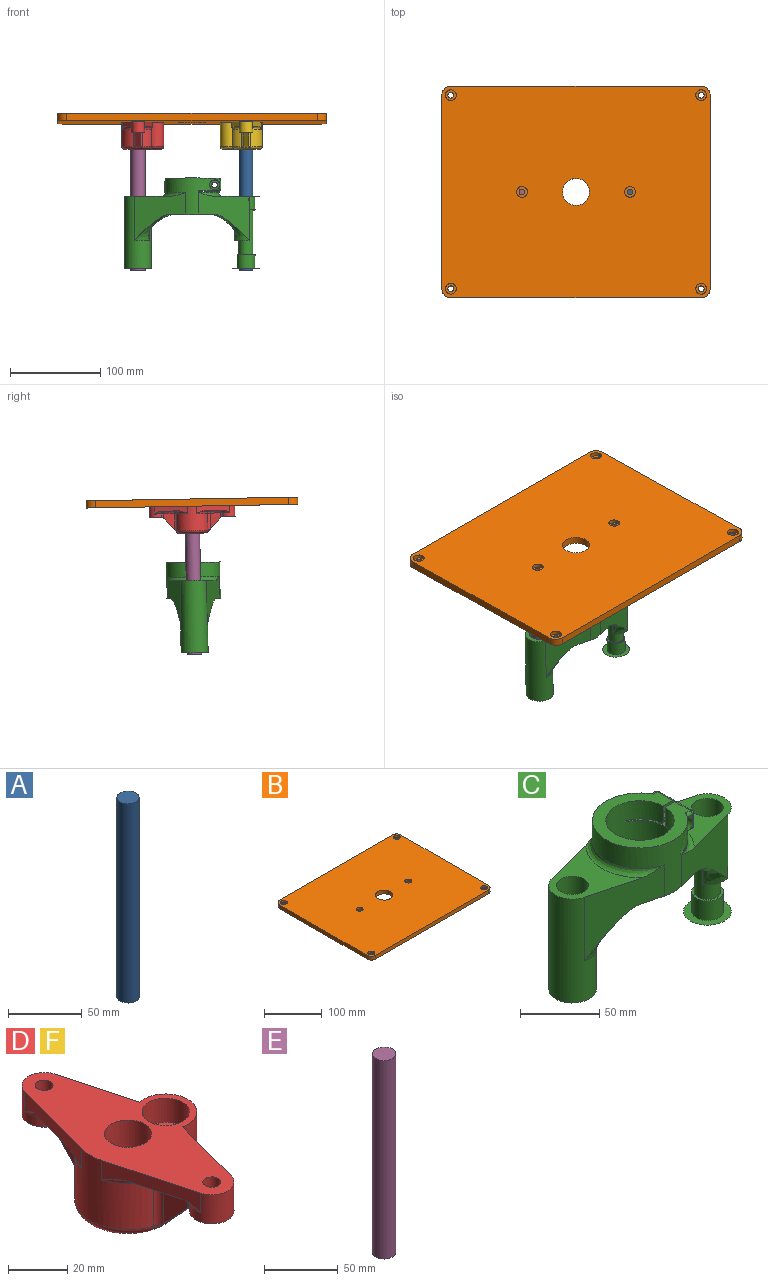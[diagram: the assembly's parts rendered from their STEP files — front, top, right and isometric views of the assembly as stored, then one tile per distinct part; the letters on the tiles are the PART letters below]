
ASSEMBLY  parts=6 mates=6
PART A: 3 faces, bbox 15x15x165 mm
  f0: cylinder r=7.5mm len=165mm, axis (0,0,1), area 7775.4mm2, adj f1,f2
  f1: plane 15x15mm, normal (0,0,1), area 176.7mm2, adj f0
  f2: plane 15x15mm, normal (0,0,-1), area 176.7mm2, adj f0
PART B: 29 faces, bbox 298x235x8 mm
  f0: plane 278x8mm, normal (0,1,0), area 2224mm2, adj f1,f12,f15,f16
  f1: cylinder r=10mm len=10mm, axis (0,0,1), area 125.7mm2, adj f0,f2,f15,f16
  f2: plane 215x8mm, normal (-1,0,0), area 1720mm2, adj f1,f3,f15,f16
  f3: cylinder r=10mm len=10mm, axis (0,0,1), area 125.7mm2, adj f2,f4,f15,f16
  f4: plane 278x8mm, normal (0,-1,0), area 2224mm2, adj f3,f5,f15,f16
  f5: cylinder r=10mm len=10mm, axis (0,0,1), area 125.7mm2, adj f4,f6,f15,f16
  f6: plane 215x8mm, normal (1,0,0), area 1720mm2, adj f5,f12,f15,f16
  f7: cylinder r=6mm len=12mm, axis (0,0,1), area 150.8mm2, adj f15,f20
  f8: cylinder r=6mm len=12mm, axis (0,0,1), area 150.8mm2, adj f15,f24
  f9: cylinder r=6mm len=12mm, axis (0,0,1), area 150.8mm2, adj f15,f22
  f10: cylinder r=6mm len=12mm, axis (0,0,1), area 150.8mm2, adj f15,f18
  f11: cylinder r=15mm len=30mm, axis (0,0,1), area 754mm2, adj f15,f16
  f12: cylinder r=10mm len=10mm, axis (0,0,1), area 125.7mm2, adj f0,f6,f15,f16
  f13: cylinder r=6mm len=12mm, axis (0,0,1), area 150.8mm2, adj f15,f26
  f14: cylinder r=6mm len=12mm, axis (0,0,1), area 150.8mm2, adj f15,f28
  f15: plane 298x235mm, normal (0,0,1), area 68558.7mm2, adj f0,f1,f2,f3,f4,f5,f6,f7
  f16: plane 298x235mm, normal (0,0,-1), area 69038.2mm2, adj f0,f1,f2,f3,f4,f5,f6,f11
  f17: cylinder r=3.25mm len=6.5mm, axis (0,0,1), area 81.7mm2, adj f16,f18
  f18: plane 12x12mm, normal (0,0,1), area 79.9mm2, adj f10,f17
  f19: cylinder r=3.25mm len=6.5mm, axis (0,0,1), area 81.7mm2, adj f16,f20
  f20: plane 12x12mm, normal (0,0,1), area 79.9mm2, adj f7,f19
  f21: cylinder r=3.25mm len=6.5mm, axis (0,0,1), area 81.7mm2, adj f16,f22
  f22: plane 12x12mm, normal (0,0,1), area 79.9mm2, adj f9,f21
  f23: cylinder r=3.25mm len=6.5mm, axis (0,0,1), area 81.7mm2, adj f16,f24
  f24: plane 12x12mm, normal (0,0,1), area 79.9mm2, adj f8,f23
  f25: cylinder r=3.25mm len=6.5mm, axis (0,0,1), area 81.7mm2, adj f16,f26
  f26: plane 12x12mm, normal (0,0,1), area 79.9mm2, adj f13,f25
  f27: cylinder r=3.25mm len=6.5mm, axis (0,0,1), area 81.7mm2, adj f16,f28
  f28: plane 12x12mm, normal (0,0,1), area 79.9mm2, adj f14,f27
PART C: 91 faces, bbox 210x148.6x160 mm
  f0: plane 4.53x2.61mm, normal (0,1,0), area 5.9mm2, adj f1,f89,f90
  f1: cylinder r=2mm len=10mm, axis (0,0,1), area 31.4mm2, adj f0,f2,f85,f86,f87,f88
  f2: plane 5.77x5mm, normal (-1,0,0), area 28.9mm2, adj f1,f3,f84,f90
  f3: plane 11.55x10mm, normal (0,1,0), area 55.4mm2, adj f2,f4,f81,f82,f83,f84,f90
  f4: cylinder r=3.15mm len=10.58mm, axis (0,-1,0), area 209.5mm2, adj f3,f5
  f5: plane 12x10.52mm, normal (0,-1,0), area 94.2mm2, adj f4,f6,f78,f79,f80,f87
  f6: plane 60x60mm, normal (0,0,1), area 1394mm2, adj f5,f7,f26,f27,f28,f78,f80,f89
  f7: plane 14x10.52mm, normal (0,1,0), area 114.4mm2, adj f6,f8,f23,f24,f25,f26,f80
  f8: plane 28.17x23mm, normal (0,0,-1), area 292.9mm2, adj f7,f9,f15,f23,f28,f80
  f9: plane 8.84x1mm, normal (1,0,0), area 8.8mm2, adj f8,f10,f28,f80
  f10: plane 58.34x23mm, normal (0,0,1), area 567.1mm2, adj f9,f11,f28,f80
  f11: plane 8.84x1mm, normal (1,0,0), area 8.8mm2, adj f10,f12,f28,f80
  f12: plane 26.17x23mm, normal (0,0,-1), area 275.7mm2, adj f11,f13,f14,f28,f79,f80
  f13: cylinder r=2mm len=13.58mm, axis (0,-1,0), area 39.5mm2, adj f12,f79,f86,f87
  f14: cylinder r=2mm len=4.77mm, axis (1,0,0), area 12.8mm2, adj f12,f28,f84,f85,f86
  f15: cylinder r=2mm len=4.83mm, axis (1,0,0), area 12.5mm2, adj f8,f16,f21,f22,f28
  f16: cylinder r=5.5mm len=11.22mm, axis (0,-1,0), area 244.7mm2, adj f15,f17,f18,f20,f21,f28
  f17: plane 11x11mm, normal (0,-1,0), area 63.9mm2, adj f16,f25
  f18: cylinder r=2mm len=10mm, axis (0,0,-1), area 29.9mm2, adj f16,f19,f20,f21,f22,f24
  f19: sphere r=2mm, area 6.3mm2, adj f18,f26,f27
  f20: plane 5x3.21mm, normal (0,-1,0), area 4.5mm2, adj f16,f18,f27
  f21: plane 2.21x1.84mm, normal (0,-1,0), area 1.7mm2, adj f15,f16,f18
  f22: sphere r=2mm, area 6.3mm2, adj f15,f18,f23
  f23: cylinder r=2mm len=13.58mm, axis (0,-1,0), area 42.7mm2, adj f7,f8,f22,f24
  f24: plane 13.58x10mm, normal (1,0,0), area 135.8mm2, adj f7,f18,f23,f26
  f25: cylinder r=3.15mm len=10.58mm, axis (0,-1,0), area 209.5mm2, adj f7,f17
  f26: cylinder r=2mm len=13.58mm, axis (0,-1,0), area 42.7mm2, adj f6,f7,f19,f24
  f27: cylinder r=2mm len=5mm, axis (-1,0,0), area 13.8mm2, adj f6,f19,f20,f28
  f28: cylinder r=30mm len=60mm, axis (0,0,-1), area 3034.8mm2, adj f6,f8,f9,f10,f11,f12,f14,f15
  f29: bspline ~67.5x30.38mm, area 420.1mm2, adj f28,f30,f50,f77
  f30: plane 52.02x50.11mm, normal (0,0,1), area 1159.2mm2, adj f29,f31,f49,f50,f77
  f31: cylinder r=15mm len=80mm, axis (0,0,-1), area 5486.3mm2, adj f30,f32,f35,f36,f37,f38,f41,f42
  f32: bspline ~53.6x37.64mm, area 288.5mm2, adj f31,f33,f35,f76,f77
  f33: plane 28.75x23.43mm, normal (0.25,0.97,0), area 477.1mm2, adj f32,f34,f35,f36,f76
  f34: cylinder r=30mm len=17.84mm, axis (0,0,-1), area 304.2mm2, adj f33,f36,f37,f76
  f35: cylinder r=5mm len=44mm, axis (0,0,-1), area 340.4mm2, adj f31,f32,f33,f36
  f36: plane 27.04x17.84mm, normal (0,0,-1), area 275.6mm2, adj f31,f33,f34,f35,f37
  f37: plane 15.65x15mm, normal (0,-1,0), area 234.8mm2, adj f31,f34,f36,f76
  f38: plane 15.65x15mm, normal (0,1,0), area 234.8mm2, adj f31,f39,f41,f76
  f39: cylinder r=30mm len=17.84mm, axis (0,0,-1), area 304.2mm2, adj f38,f40,f41,f76
  f40: plane 28.75x23.43mm, normal (0.25,-0.97,0), area 477.1mm2, adj f39,f41,f42,f43,f76
  f41: plane 27.04x17.84mm, normal (0,0,-1), area 275.6mm2, adj f31,f38,f39,f40,f42
  f42: cylinder r=5mm len=44mm, axis (0,0,-1), area 340.4mm2, adj f31,f40,f41,f43
  f43: bspline ~53.6x37.9mm, area 288.4mm2, adj f31,f40,f42,f50,f76
  f44: plane 30x30mm, normal (0,0,-1), area 392.7mm2, adj f31,f45
  f45: cylinder r=10mm len=20mm, axis (0,0,-1), area 942.5mm2, adj f44,f46
  f46: plane 20x20mm, normal (0,0,-1), area 100.3mm2, adj f45,f47
  f47: cylinder r=8.25mm len=50mm, axis (0,0,-1), area 2591.8mm2, adj f46,f48
  f48: plane 20x20mm, normal (0,0,1), area 100.3mm2, adj f47,f49
  f49: cylinder r=10mm len=20mm, axis (0,0,-1), area 942.5mm2, adj f30,f48
  f50: plane 58.2x54.95mm, normal (-0.25,0.97,0), area 1659.2mm2, adj f28,f29,f30,f31,f43,f76
  f51: plane 58.2x54.95mm, normal (0.25,0.97,0), area 1659.2mm2, adj f28,f52,f65,f66,f74,f76
  f52: bspline ~51.76x37.9mm, area 288.4mm2, adj f51,f53,f64,f65,f76
  f53: plane 28.75x23.43mm, normal (-0.25,-0.97,0), area 477.1mm2, adj f52,f54,f63,f64,f76
  f54: cylinder r=30mm len=17.84mm, axis (0,0,-1), area 304.2mm2, adj f53,f55,f63,f76
  f55: plane 90x75.65mm, normal (0,1,0), area 273.1mm2, adj f54,f56,f63,f65,f76
  f56: bspline ~15.41x15mm, area 169mm2, adj f55,f57,f65,f76
  f57: plane 30.53x16.18mm, normal (0,-1,0), area 273.1mm2, adj f56,f58,f62,f65,f76
  f58: cylinder r=30mm len=17.84mm, axis (0,0,-1), area 304.2mm2, adj f57,f59,f62,f76
  f59: plane 28.75x23.43mm, normal (-0.25,0.97,0), area 477.1mm2, adj f58,f60,f61,f62,f76
  f60: bspline ~53.6x37.9mm, area 288.4mm2, adj f59,f61,f65,f75,f76
  f61: cylinder r=5mm len=44mm, axis (0,0,-1), area 340.4mm2, adj f59,f60,f62,f65
  f62: plane 27.04x17.84mm, normal (0,0,-1), area 275.6mm2, adj f57,f58,f59,f61,f65
  f63: plane 87.04x77.84mm, normal (0,0,-1), area 275.6mm2, adj f53,f54,f55,f64,f65
  f64: cylinder r=5mm len=44mm, axis (0,0,-1), area 340.4mm2, adj f52,f53,f63,f65
  f65: cylinder r=15mm len=49mm, axis (0,0,-1), area 984.1mm2, adj f51,f52,f55,f56,f57,f60,f61,f62
  f66: plane 52.02x50.11mm, normal (0,0,1), area 1159.4mm2, adj f51,f65,f67,f74,f75
  f67: cylinder r=10mm len=20mm, axis (0,0,-1), area 942.5mm2, adj f66,f68
  f68: plane 20x20mm, normal (0,0,1), area 100.3mm2, adj f67,f69
  f69: cylinder r=8.25mm len=50mm, axis (0,0,-1), area 2591.8mm2, adj f68,f70
  f70: plane 20x20mm, normal (0,0,-1), area 100.3mm2, adj f69,f71
  f71: cylinder r=10mm len=20mm, axis (0,0,-1), area 942.5mm2, adj f70,f72
  f72: plane 90x90mm, normal (0,0,-1), area 392.7mm2, adj f71,f73
  f73: cylinder r=15mm len=3.59mm, axis (0,0,-1), area 0mm2, adj f72
  f74: bspline ~67.5x30.38mm, area 420.1mm2, adj f28,f51,f66,f75
  f75: plane 58.2x54.95mm, normal (0.25,-0.97,0), area 1659.2mm2, adj f28,f60,f65,f66,f74,f76
  f76: plane 75.66x60.01mm, normal (0,0,-1), area 1580.8mm2, adj f28,f31,f32,f33,f34,f37,f38,f39
  f77: plane 58.2x54.95mm, normal (-0.25,-0.97,0), area 1659.1mm2, adj f28,f29,f30,f31,f32,f76
  f78: cylinder r=2mm len=13.58mm, axis (0,-1,0), area 42.7mm2, adj f5,f6,f87,f88
  f79: cylinder r=2mm len=10.71mm, axis (-1,0,0), area 30.2mm2, adj f5,f12,f13,f80
  f80: cylinder r=21.5mm len=43mm, axis (0,0,-1), area 5321.4mm2, adj f5,f6,f7,f8,f9,f10,f11,f12
  f81: plane 10.78x5mm, normal (0.5,0,-0.87), area 47mm2, adj f3,f28,f82,f90
  f82: plane 10.78x5.77mm, normal (1,0,0), area 62.2mm2, adj f3,f28,f81,f83
  f83: plane 10.78x5mm, normal (0.5,0,0.87), area 47mm2, adj f3,f28,f82,f84
  f84: plane 5.1x5.1mm, normal (-0.5,0,0.87), area 28.6mm2, adj f2,f3,f14,f28,f83,f85
  f85: plane 2.79x1.61mm, normal (0,1,0), area 2.3mm2, adj f1,f14,f84
  f86: sphere r=2mm, area 4mm2, adj f1,f13,f14
  f87: plane 13.58x10mm, normal (1,0,0), area 135.8mm2, adj f1,f5,f13,f78
  f88: sphere r=2mm, area 4mm2, adj f1,f78,f89
  f89: cylinder r=2mm len=4.99mm, axis (1,0,0), area 13.9mm2, adj f0,f6,f28,f88,f90
  f90: plane 5x5mm, normal (-0.5,0,-0.87), area 28.9mm2, adj f0,f2,f3,f28,f81,f89
PART D: 78 faces, bbox 54.4x95.9x31 mm
  f0: cylinder r=18mm len=19mm, axis (0,0,1), area 235.7mm2, adj f15,f45,f49,f52
  f1: cylinder r=18mm len=34.5mm, axis (0,0,1), area 952.7mm2, adj f16,f18,f22,f45,f58,f60,f65,f68
  f2: cylinder r=5.1mm len=20mm, axis (0,0,1), area 640.9mm2, adj f17,f43
  f3: plane 19.72x8.53mm, normal (0,0,-1), area 83.9mm2, adj f21,f71,f73,f74
  f4: plane 19.72x8.53mm, normal (0,0,-1), area 83.9mm2, adj f22,f62,f65,f66
  f5: cylinder r=7.5mm len=15mm, axis (0,0,1), area 308.6mm2, adj f16,f21,f22,f31,f62,f63,f70,f71
  f6: plane 19.72x8.53mm, normal (0,0,-1), area 83.9mm2, adj f19,f46,f49,f50
  f7: plane 5.6x4mm, normal (0.97,0.25,0), area 23.1mm2, adj f8,f12,f24,f33
  f8: plane 4.13x4.03mm, normal (0.7,-0.72,0), area 23.1mm2, adj f7,f9,f24,f33
  f9: plane 5.56x4mm, normal (-0.27,-0.96,0), area 23.1mm2, adj f8,f10,f24,f33
  f10: plane 5.6x4mm, normal (-0.97,-0.25,0), area 23.1mm2, adj f9,f11,f24,f33
  f11: plane 4.13x4.03mm, normal (-0.7,0.72,0), area 23.1mm2, adj f10,f12,f24,f33
  f12: plane 5.56x4mm, normal (0.27,0.96,0), area 23.1mm2, adj f7,f11,f24,f33
  f13: cylinder r=18mm len=19mm, axis (0,0,1), area 235.7mm2, adj f15,f45,f74,f76
  f14: cylinder r=8mm len=30mm, axis (0,0,1), area 1508mm2, adj f16,f17
  f15: cylinder r=10.5mm len=27mm, axis (0,0,1), area 1045.3mm2, adj f0,f13,f16,f19,f21,f44,f49,f74
  f16: plane 95x46.5mm, normal (0,0,1), area 2019.9mm2, adj f1,f5,f14,f15,f18,f19,f21,f22
  f17: plane 40.5x30mm, normal (0,0,-1), area 562.5mm2, adj f2,f14,f44,f45
  f18: plane 38.12x11mm, normal (-0.96,0.26,0), area 213.5mm2, adj f1,f16,f20,f23,f55,f58
  f19: plane 32.56x9.49mm, normal (0.96,0.26,0), area 173.9mm2, adj f6,f15,f16,f23,f46,f49
  f20: plane 19.72x8.53mm, normal (0,0,-1), area 83.9mm2, adj f18,f55,f57,f58
  f21: plane 32.56x9.49mm, normal (0.96,-0.26,0), area 173.9mm2, adj f3,f5,f15,f16,f71,f74
  f22: plane 38.12x11mm, normal (-0.96,-0.26,0), area 213.5mm2, adj f1,f4,f5,f16,f62,f65
  f23: cylinder r=7.5mm len=15mm, axis (0,0,1), area 308.6mm2, adj f16,f18,f19,f24,f46,f47,f54,f55
  f24: plane 15x14.67mm, normal (0,0,-1), area 89.1mm2, adj f7,f8,f9,f10,f11,f12,f23,f41
  f25: plane 5.56x4mm, normal (-0.27,0.96,0), area 23.1mm2, adj f26,f30,f31,f35
  f26: plane 4.13x4.03mm, normal (0.7,0.72,0), area 23.1mm2, adj f25,f27,f31,f35
  f27: plane 5.6x4mm, normal (0.97,-0.25,0), area 23.1mm2, adj f26,f28,f31,f35
  f28: plane 5.56x4mm, normal (0.27,-0.96,0), area 23.1mm2, adj f27,f29,f31,f35
  f29: plane 4.13x4.03mm, normal (-0.7,-0.72,0), area 23.1mm2, adj f28,f30,f31,f35
  f30: plane 5.6x4mm, normal (-0.97,0.25,0), area 23.1mm2, adj f25,f29,f31,f35
  f31: plane 15x14.67mm, normal (0,0,-1), area 89.1mm2, adj f5,f25,f26,f27,f28,f29,f30,f40
  f32: cylinder r=3mm len=8mm, axis (0,0,1), area 150.8mm2, adj f16,f33
  f33: plane 11.19x11.11mm, normal (0,0,-1), area 58.3mm2, adj f7,f8,f9,f10,f11,f12,f32
  f34: cylinder r=3mm len=8mm, axis (0,0,1), area 150.8mm2, adj f16,f35
  f35: plane 11.19x11.11mm, normal (0,0,-1), area 58.3mm2, adj f25,f26,f27,f28,f29,f30,f34
  f36: plane 17.79x11.55mm, normal (1,0,0), area 129.9mm2, adj f41,f47,f50,f52
  f37: plane 17.79x11.55mm, normal (-1,0,0), area 129.9mm2, adj f41,f54,f57,f60
  f38: plane 17.79x11.55mm, normal (1,0,0), area 129.9mm2, adj f40,f70,f73,f76
  f39: plane 17.79x11.55mm, normal (-1,0,0), area 129.9mm2, adj f40,f63,f66,f68
  f40: cone r=33mm half-angle=43.2deg, axis (0,0,1), area 144.3mm2, adj f31,f38,f39,f45,f63,f68,f69,f70
  f41: cone r=33mm half-angle=43.2deg, axis (0,0,1), area 144.3mm2, adj f24,f36,f37,f45,f47,f52,f53,f54
  f42: cylinder r=8mm len=16mm, axis (0,0,1), area 502.7mm2, adj f16,f43
  f43: plane 16x16mm, normal (0,0,1), area 119.3mm2, adj f2,f42
  f44: torus R=7.5mm, axis (0,0,1), area 178.8mm2, adj f15,f17,f45
  f45: torus R=15mm, axis (0,0,1), area 390.4mm2, adj f0,f1,f13,f17,f40,f41,f44,f53
  f46: torus R=10.5mm, axis (0,0,1), area 33.1mm2, adj f6,f19,f23,f48
  f47: cylinder r=3mm len=5.57mm, axis (0,0,1), area 12.7mm2, adj f23,f24,f36,f41,f48
  f48: sphere r=3mm, area 8.7mm2, adj f46,f47,f50
  f49: torus R=21mm, axis (0,0,1), area 57.7mm2, adj f0,f6,f15,f19,f51
  f50: cylinder r=3mm len=11.26mm, axis (0,-1,0), area 53.1mm2, adj f6,f36,f48,f51
  f51: sphere r=3mm, area 16.7mm2, adj f49,f50,f52
  f52: cylinder r=3mm len=19mm, axis (0,0,1), area 71.8mm2, adj f0,f36,f41,f51,f53
  f53: bspline ~3.97x3.35mm, area 1.7mm2, adj f41,f45,f52
  f54: cylinder r=3mm len=5.57mm, axis (0,0,1), area 12.7mm2, adj f23,f24,f37,f41,f56
  f55: torus R=10.5mm, axis (0,0,1), area 33.1mm2, adj f18,f20,f23,f56
  f56: sphere r=3mm, area 5.5mm2, adj f54,f55,f57
  f57: cylinder r=3mm len=11.26mm, axis (0,-1,0), area 53.1mm2, adj f20,f37,f56,f59
  f58: torus R=21mm, axis (0,0,1), area 66.3mm2, adj f1,f18,f20,f59
  f59: sphere r=3mm, area 11.5mm2, adj f57,f58,f60
  f60: cylinder r=3mm len=19mm, axis (0,0,1), area 71.8mm2, adj f1,f37,f41,f59,f61
  f61: bspline ~3.97x3.35mm, area 1.7mm2, adj f41,f45,f60
  f62: torus R=10.5mm, axis (0,0,1), area 33.1mm2, adj f4,f5,f22,f64
  f63: cylinder r=3mm len=5.57mm, axis (0,0,1), area 12.7mm2, adj f5,f31,f39,f40,f64
  f64: sphere r=3mm, area 8.7mm2, adj f62,f63,f66
  f65: torus R=21mm, axis (0,0,1), area 66.3mm2, adj f1,f4,f22,f67
  f66: cylinder r=3mm len=11.26mm, axis (0,1,0), area 53.1mm2, adj f4,f39,f64,f67
  f67: sphere r=3mm, area 7.3mm2, adj f65,f66,f68
  f68: cylinder r=3mm len=19mm, axis (0,0,1), area 71.8mm2, adj f1,f39,f40,f67,f69
  f69: bspline ~3.97x3.35mm, area 1.7mm2, adj f40,f45,f68
  f70: cylinder r=3mm len=5.57mm, axis (0,0,1), area 12.7mm2, adj f5,f31,f38,f40,f72
  f71: torus R=10.5mm, axis (0,0,1), area 33.1mm2, adj f3,f5,f21,f72
  f72: sphere r=3mm, area 8.7mm2, adj f70,f71,f73
  f73: cylinder r=3mm len=11.26mm, axis (0,1,0), area 53.1mm2, adj f3,f38,f72,f75
  f74: torus R=21mm, axis (0,0,1), area 57.7mm2, adj f3,f13,f15,f21,f75
  f75: sphere r=3mm, area 11.5mm2, adj f73,f74,f76
  f76: cylinder r=3mm len=19mm, axis (0,0,1), area 71.8mm2, adj f13,f38,f40,f75,f77
  f77: bspline ~3.97x3.35mm, area 1.7mm2, adj f40,f45,f76
PART E: 3 faces, bbox 16x16x165 mm
  f0: cylinder r=8mm len=165mm, axis (0,0,1), area 8293.8mm2, adj f1,f2
  f1: plane 16x16mm, normal (0,0,1), area 201.1mm2, adj f0
  f2: plane 16x16mm, normal (0,0,-1), area 201.1mm2, adj f0
PART F: same geometry as D
PLACE A rot(axis=(-1,0,0),1deg) t=(-29.19,-81.53,61.47)mm
PLACE B rot(axis=(-1,0,0),1deg) t=(-29.19,-81.53,61.47)mm fixed
PLACE C rot(axis=(-1,0,0),1deg) t=(-29.19,-82.45,8.98)mm
PLACE D rot(axis=(-1,0,0),1deg) t=(-29.19,-81.53,61.47)mm
PLACE E rot(axis=(-1,0,0),1deg) t=(-29.19,-81.53,61.47)mm
PLACE F rot(axis=(0,0.01,1),180deg) t=(-29.19,-81.53,61.47)mm
MATE fastened D.f14 <-> B.f25  axis (0,0.02,1) through (-89.19,-81.53,61.47)mm
MATE cylindrical A.f0 <-> C.f69  axis (0,0.02,1) through (30.81,-82.97,-21.02)mm
MATE fastened B.f25 <-> E.f0  axis (0,-0.02,-1) through (-89.19,-81.53,61.47)mm
MATE fastened B.f27 <-> F.f14  axis (0,-0.02,-1) through (30.81,-81.53,61.47)mm
MATE fastened A.f0 <-> B.f27  axis (0,0.02,1) through (30.81,-81.53,61.47)mm
MATE cylindrical E.f0 <-> C.f47  axis (0,0.02,1) through (-89.19,-82.97,-21.02)mm
